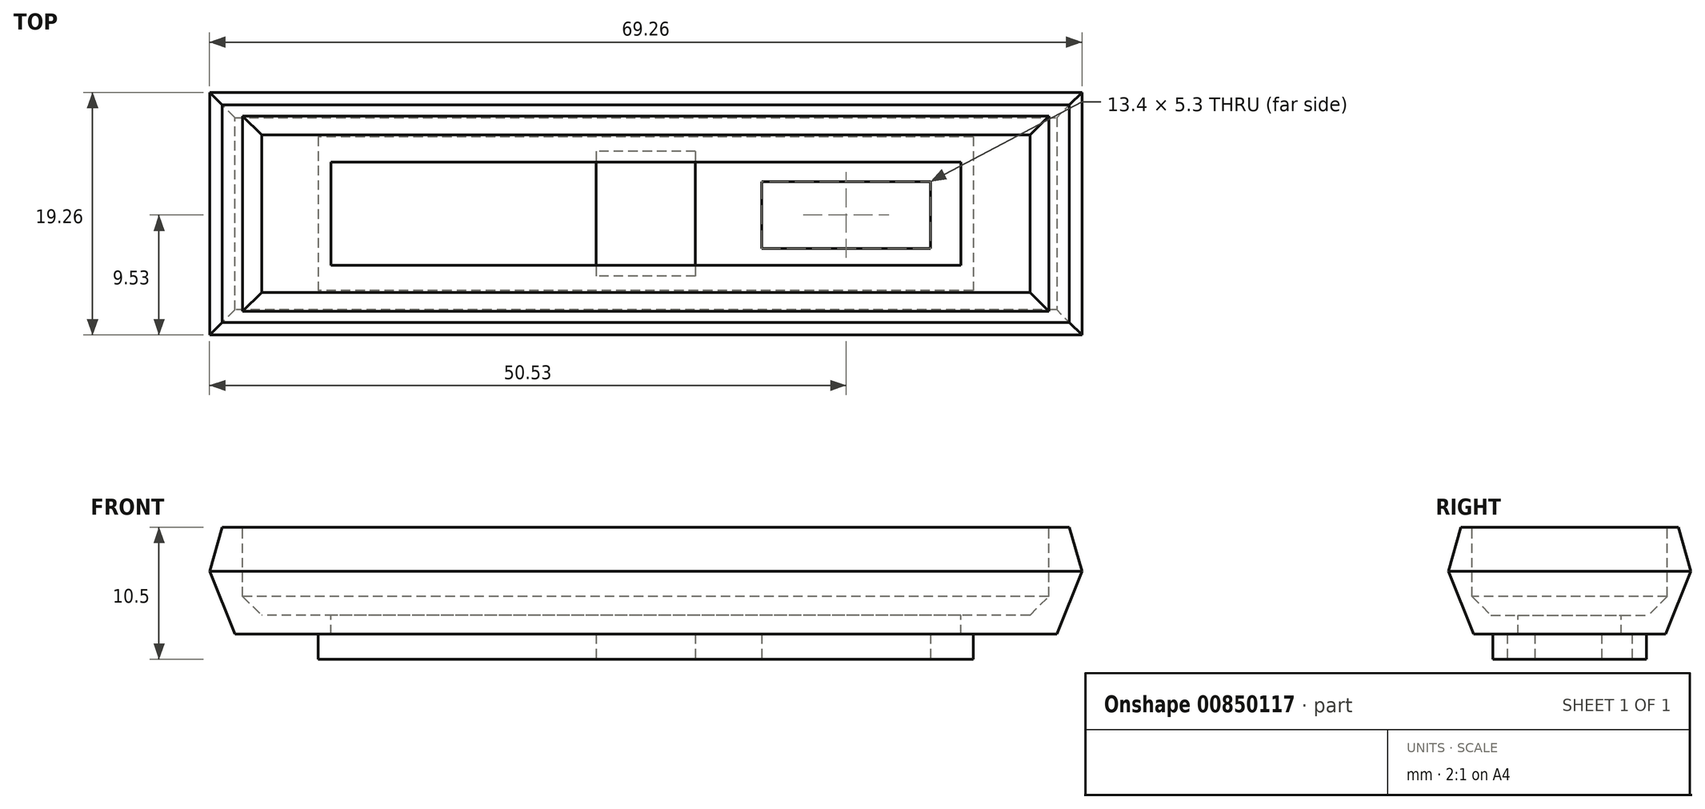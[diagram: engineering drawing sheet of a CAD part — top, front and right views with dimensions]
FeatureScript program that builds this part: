
annotation { "Feature Type Name" : "Feature", "Feature Type Description" : "" }
export const myFeature = defineFeature(function(context is Context, id is Id, definition is map)
    precondition{}
    {
        {
            var Q0;
            Q0=qCreatedBy(makeId("Top.planeOp"),FACE);
            var sketch = newSketch(context, id + "F0", { "sketchPlane" : qUnion([Q0])});
            skLineSegment(sketch, "E0.bottom", {"start": v(34.62, -9.62) * mm, "end": v(-34.62, -9.63) * mm});
            skLineSegment(sketch, "E0.top", {"start": v(34.62, 9.63) * mm, "end": v(-34.62, 9.62) * mm});
            skLineSegment(sketch, "E0.left", {"start": v(34.62, -9.62) * mm, "end": v(34.62, 9.63) * mm});
            skLineSegment(sketch, "E0.right", {"start": v(-34.62, -9.63) * mm, "end": v(-34.62, 9.62) * mm});
            skPoint(sketch, "E0.middle", {"position": v(0, 0) * mm});
            skSolve(sketch);
        }
        {
            var Q0;
            Q0=makeQuery(id+"F0.imprint","IMPRINT",FACE,{"disambiguationData":[TD([[makeQuery(id+"F0.imprint","IMPRINT",EDGE,{"derivedFrom":sQuery(id+"F0.wireOp",EDGE,"E0.bottom")}),-1.0]])]});
            extrude(context, id + "F1", {"entities" : qUnion([Q0]), "depth" : 8.5 * mm, "offsetDistance" : 25 * mm});
        }
        {
            var Q0;
            Q0=makeQuery(id+"F1.opExtrude","CAP_FACE",FACE,{"disambiguationData":[OSD([sQuery(id+"F0.wireOp",EDGE,"E0.bottom"),sQuery(id+"F0.wireOp",EDGE,"E0.top"),sQuery(id+"F0.wireOp",EDGE,"E0.left"),sQuery(id+"F0.wireOp",EDGE,"E0.right")])],"isStart":false});
            var sketch = newSketch(context, id + "F2", { "sketchPlane" : qUnion([Q0])});
            skLineSegment(sketch, "E1.bottom", {"start": v(32, -7.75) * mm, "end": v(-32, -7.75) * mm});
            skLineSegment(sketch, "E1.top", {"start": v(32, 7.75) * mm, "end": v(-32, 7.75) * mm});
            skLineSegment(sketch, "E1.left", {"start": v(32, -7.75) * mm, "end": v(32, 7.75) * mm});
            skLineSegment(sketch, "E1.right", {"start": v(-32, -7.75) * mm, "end": v(-32, 7.75) * mm});
            skPoint(sketch, "E1.middle", {"position": v(0, 0) * mm});
            skLineSegment(sketch, "E2.bottom", {"start": v(33, -8.75) * mm, "end": v(-33, -8.75) * mm});
            skLineSegment(sketch, "E2.top", {"start": v(33, 8.75) * mm, "end": v(-33, 8.75) * mm});
            skLineSegment(sketch, "E2.left", {"start": v(33, -8.75) * mm, "end": v(33, 8.75) * mm});
            skLineSegment(sketch, "E2.right", {"start": v(-33, -8.75) * mm, "end": v(-33, 8.75) * mm});
            skSolve(sketch);
        }
        {
            var Q0;
            Q0=makeQuery(id+"F1.opExtrude","CAP_EDGE",EDGE,{"disambiguationData":[OSD([sQuery(id+"F0.wireOp",EDGE,"E0.right")])],"isStart":false});
            var Q1;
            Q1=makeQuery(id+"F1.opExtrude","CAP_EDGE",EDGE,{"disambiguationData":[OSD([sQuery(id+"F0.wireOp",EDGE,"E0.bottom")])],"isStart":false});
            var Q2;
            Q2=makeQuery(id+"F1.opExtrude","CAP_EDGE",EDGE,{"disambiguationData":[OSD([sQuery(id+"F0.wireOp",EDGE,"E0.left")])],"isStart":false});
            var Q3;
            Q3=makeQuery(id+"F1.opExtrude","CAP_EDGE",EDGE,{"disambiguationData":[OSD([sQuery(id+"F0.wireOp",EDGE,"E0.top")])],"isStart":false});
            chamfer(context, id + "F3", {"entities" : qUnion([Q0, Q1, Q2, Q3]), "chamferType" : ChamferType.TWO_OFFSETS, "width1" : 3.5 * mm, "oppositeDirection" : false, "width2" : 1 * mm, "tangentPropagation" : true});
        }
        {
            var Q0;
            Q0=makeQuery(id+"F1.opExtrude","CAP_EDGE",EDGE,{"disambiguationData":[OSD([sQuery(id+"F0.wireOp",EDGE,"E0.right")])],"isStart":true});
            var Q1;
            Q1=makeQuery(id+"F1.opExtrude","CAP_EDGE",EDGE,{"disambiguationData":[OSD([sQuery(id+"F0.wireOp",EDGE,"E0.bottom")])],"isStart":true});
            var Q2;
            Q2=makeQuery(id+"F1.opExtrude","CAP_EDGE",EDGE,{"disambiguationData":[OSD([sQuery(id+"F0.wireOp",EDGE,"E0.top")])],"isStart":true});
            var Q3;
            Q3=makeQuery(id+"F1.opExtrude","CAP_EDGE",EDGE,{"disambiguationData":[OSD([sQuery(id+"F0.wireOp",EDGE,"E0.left")])],"isStart":true});
            chamfer(context, id + "F4", {"entities" : qUnion([Q0, Q1, Q2, Q3]), "chamferType" : ChamferType.TWO_OFFSETS, "width1" : 2 * mm, "oppositeDirection" : false, "width2" : 5 * mm, "tangentPropagation" : true});
        }
        {
            var Q0;
            Q0=makeQuery(id+"F2.imprint","IMPRINT",FACE,{"disambiguationData":[TD([[makeQuery(id+"F2.imprint","IMPRINT",EDGE,{"derivedFrom":sQuery(id+"F2.wireOp",EDGE,"E1.bottom")}),-1.0]])]});
            extrude(context, id + "F5", {"entities" : qUnion([Q0]), "operationType" : NewBodyOperationType.REMOVE, "oppositeDirection" : true, "depth" : 7 * mm, "offsetDistance" : 25 * mm});
        }
        {
            var Q0;
            Q0=makeQuery(id+"F1.opExtrude","CAP_FACE",FACE,{"disambiguationData":[OSD([sQuery(id+"F0.wireOp",EDGE,"E0.bottom"),sQuery(id+"F0.wireOp",EDGE,"E0.top"),sQuery(id+"F0.wireOp",EDGE,"E0.left"),sQuery(id+"F0.wireOp",EDGE,"E0.right")])],"isStart":true});
            var sketch = newSketch(context, id + "F6", { "sketchPlane" : qUnion([Q0])});
            skLineSegment(sketch, "E3.bottom", {"start": v(26, -6.1) * mm, "end": v(-26, -6.1) * mm});
            skLineSegment(sketch, "E3.top", {"start": v(26, 6.1) * mm, "end": v(-26, 6.1) * mm});
            skLineSegment(sketch, "E3.left", {"start": v(26, -6.1) * mm, "end": v(26, 6.1) * mm});
            skLineSegment(sketch, "E3.right", {"start": v(-26, -6.1) * mm, "end": v(-26, 6.1) * mm});
            skPoint(sketch, "E3.middle", {"position": v(0, 0) * mm});
            skSolve(sketch);
        }
        {
            var Q0;
            Q0=makeQuery(id+"F6.imprint","IMPRINT",FACE,{"disambiguationData":[TD([[makeQuery(id+"F6.imprint","IMPRINT",EDGE,{"derivedFrom":sQuery(id+"F6.wireOp",EDGE,"E3.bottom")}),-1.0]])]});
            extrude(context, id + "F7", {"entities" : qUnion([Q0]), "operationType" : NewBodyOperationType.ADD, "depth" : 2 * mm, "offsetDistance" : 25 * mm});
        }
        {
            var Q0;
            Q0=makeQuery(id+"F7.opExtrude","CAP_FACE",FACE,{"disambiguationData":[OSD([sQuery(id+"F6.wireOp",EDGE,"E3.bottom"),sQuery(id+"F6.wireOp",EDGE,"E3.top"),sQuery(id+"F6.wireOp",EDGE,"E3.left"),sQuery(id+"F6.wireOp",EDGE,"E3.right")])],"isStart":false});
            var sketch = newSketch(context, id + "F8", { "sketchPlane" : qUnion([Q0])});
            skLineSegment(sketch, "E4.bottom", {"start": v(3.95, -4.95) * mm, "end": v(-3.95, -4.95) * mm});
            skLineSegment(sketch, "E4.top", {"start": v(3.95, 4.95) * mm, "end": v(-3.95, 4.95) * mm});
            skLineSegment(sketch, "E4.left", {"start": v(3.95, -4.95) * mm, "end": v(3.95, 4.95) * mm});
            skLineSegment(sketch, "E4.right", {"start": v(-3.95, -4.95) * mm, "end": v(-3.95, 4.95) * mm});
            skPoint(sketch, "E4.middle", {"position": v(0, 0) * mm});
            skLineSegment(sketch, "E5.bottom", {"start": v(-26, 6.1) * mm, "end": v(-22.6, 6.1) * mm});
            skLineSegment(sketch, "E5.top", {"start": v(-26, -6.1) * mm, "end": v(-22.6, -6.1) * mm});
            skLineSegment(sketch, "E5.left", {"start": v(-26, 6.1) * mm, "end": v(-26, -6.1) * mm});
            skLineSegment(sketch, "E5.right", {"start": v(-22.6, 6.1) * mm, "end": v(-22.6, -6.1) * mm});
            skLineSegment(sketch, "E6.bottom", {"start": v(-22.6, 6.1) * mm, "end": v(15.72, 6.1) * mm});
            skLineSegment(sketch, "E6.top", {"start": v(-22.6, 2.75) * mm, "end": v(15.72, 2.75) * mm});
            skLineSegment(sketch, "E6.left", {"start": v(-22.6, 6.1) * mm, "end": v(-22.6, 2.75) * mm});
            skLineSegment(sketch, "E6.right", {"start": v(15.72, 6.1) * mm, "end": v(15.72, 2.75) * mm});
            skLineSegment(sketch, "E7.bottom", {"start": v(26, 6.1) * mm, "end": v(22.6, 6.1) * mm});
            skLineSegment(sketch, "E7.top", {"start": v(26, -6.1) * mm, "end": v(22.6, -6.1) * mm});
            skLineSegment(sketch, "E7.left", {"start": v(26, 6.1) * mm, "end": v(26, -6.1) * mm});
            skLineSegment(sketch, "E7.right", {"start": v(22.6, 6.1) * mm, "end": v(22.6, -6.1) * mm});
            skLineSegment(sketch, "E8.bottom", {"start": v(15.72, 2.75) * mm, "end": v(22.6, 2.75) * mm});
            skLineSegment(sketch, "E8.top", {"start": v(15.72, 6.1) * mm, "end": v(22.6, 6.1) * mm});
            skLineSegment(sketch, "E8.left", {"start": v(15.72, 2.75) * mm, "end": v(15.72, 6.1) * mm});
            skLineSegment(sketch, "E8.right", {"start": v(22.6, 2.75) * mm, "end": v(22.6, 6.1) * mm});
            skLineSegment(sketch, "E9.bottom", {"start": v(22.6, 2.75) * mm, "end": v(9.2, 2.75) * mm});
            skLineSegment(sketch, "E9.top", {"start": v(22.6, -2.55) * mm, "end": v(9.2, -2.55) * mm});
            skLineSegment(sketch, "E9.left", {"start": v(22.6, 2.75) * mm, "end": v(22.6, -2.55) * mm});
            skLineSegment(sketch, "E9.right", {"start": v(9.2, 2.75) * mm, "end": v(9.2, -2.55) * mm});
            skLineSegment(sketch, "E10.bottom", {"start": v(-22.6, 2.75) * mm, "end": v(-9.2, 2.75) * mm});
            skLineSegment(sketch, "E10.top", {"start": v(-22.6, -2.65) * mm, "end": v(-9.2, -2.65) * mm});
            skLineSegment(sketch, "E10.left", {"start": v(-22.6, 2.75) * mm, "end": v(-22.6, -2.65) * mm});
            skLineSegment(sketch, "E10.right", {"start": v(-9.2, 2.75) * mm, "end": v(-9.2, -2.65) * mm});
            skSolve(sketch);
        }
        {
            var Q0;
            Q0=makeQuery(id+"F8.imprint","IMPRINT",FACE,{"disambiguationData":[TD([[makeQuery(id+"F8.imprint","IMPRINT",EDGE,{"derivedFrom":sQuery(id+"F8.wireOp",EDGE,"E4.bottom")}),-1.0]])]});
            var Q1;
            {var subQ0=sQuery(id+"F8.wireOp",EDGE,"E4.top");Q1=makeQuery(id+"F8.imprint","IMPRINT",FACE,{"disambiguationData":[TD([[makeQuery(id+"F8.imprint","IMPRINT",EDGE,{"derivedFrom":subQ0}),1.0]])]});}
            extrude(context, id + "F9", {"entities" : qUnion([Q0, Q1]), "operationType" : NewBodyOperationType.REMOVE, "oppositeDirection" : true, "depth" : 2 * mm, "offsetDistance" : 25 * mm});
        }
        {
            var Q0;
            Q0=makeQuery(id+"F8.imprint","IMPRINT",FACE,{"disambiguationData":[TD([[makeQuery(id+"F8.imprint","IMPRINT",EDGE,{"derivedFrom":sQuery(id+"F8.wireOp",EDGE,"E10.bottom")}),-1.0]])]});
            var Q1;
            Q1=makeQuery(id+"F8.imprint","IMPRINT",FACE,{"disambiguationData":[TD([[makeQuery(id+"F8.imprint","IMPRINT",EDGE,{"derivedFrom":sQuery(id+"F8.wireOp",EDGE,"E9.top")}),-1.0]])]});
            extrude(context, id + "F10", {"entities" : qUnion([Q0, Q1]), "operationType" : NewBodyOperationType.REMOVE, "oppositeDirection" : true, "depth" : 25 * mm, "offsetDistance" : 25 * mm});
        }
        {
            var Q0;
            Q0=makeQuery(id+"F5.boolean.opBoolean","COPY",FACE,{"derivedFrom":makeQuery(id+"F5.opExtrude","CAP_FACE",FACE,{"disambiguationData":[OSD([sQuery(id+"F2.wireOp",EDGE,"E1.bottom"),sQuery(id+"F2.wireOp",EDGE,"E1.top"),sQuery(id+"F2.wireOp",EDGE,"E1.left"),sQuery(id+"F2.wireOp",EDGE,"E1.right")])],"isStart":false})});
            var sketch = newSketch(context, id + "F11", { "sketchPlane" : qUnion([Q0])});
            skLineSegment(sketch, "E11.bottom", {"start": v(25, -4.1) * mm, "end": v(-25, -4.1) * mm});
            skLineSegment(sketch, "E11.top", {"start": v(25, 4.1) * mm, "end": v(-25, 4.1) * mm});
            skLineSegment(sketch, "E11.left", {"start": v(25, -4.1) * mm, "end": v(25, 4.1) * mm});
            skLineSegment(sketch, "E11.right", {"start": v(-25, -4.1) * mm, "end": v(-25, 4.1) * mm});
            skPoint(sketch, "E11.middle", {"position": v(0, 0) * mm});
            skSolve(sketch);
        }
        {
            var Q0;
            Q0=makeQuery(id+"F11.imprint","IMPRINT",FACE,{"disambiguationData":[TD([[makeQuery(id+"F11.imprint","IMPRINT",EDGE,{"derivedFrom":sQuery(id+"F11.wireOp",EDGE,"E11.bottom")}),-1.0]])]});
            extrude(context, id + "F12", {"entities" : qUnion([Q0]), "operationType" : NewBodyOperationType.REMOVE, "oppositeDirection" : true, "depth" : 1.5 * mm, "offsetDistance" : 25 * mm});
        }
        {
            var Q0;
            Q0=makeQuery(id+"F5.boolean.opBoolean","COPY",EDGE,{"derivedFrom":makeQuery(id+"F5.opExtrude","CAP_EDGE",EDGE,{"disambiguationData":[OSD([sQuery(id+"F2.wireOp",EDGE,"E1.right")])],"isStart":false})});
            var Q1;
            Q1=makeQuery(id+"F5.boolean.opBoolean","COPY",EDGE,{"derivedFrom":makeQuery(id+"F5.opExtrude","CAP_EDGE",EDGE,{"disambiguationData":[OSD([sQuery(id+"F2.wireOp",EDGE,"E1.top")])],"isStart":false})});
            var Q2;
            Q2=makeQuery(id+"F5.boolean.opBoolean","COPY",EDGE,{"derivedFrom":makeQuery(id+"F5.opExtrude","CAP_EDGE",EDGE,{"disambiguationData":[OSD([sQuery(id+"F2.wireOp",EDGE,"E1.left")])],"isStart":false})});
            var Q3;
            Q3=makeQuery(id+"F5.boolean.opBoolean","COPY",EDGE,{"derivedFrom":makeQuery(id+"F5.opExtrude","CAP_EDGE",EDGE,{"disambiguationData":[OSD([sQuery(id+"F2.wireOp",EDGE,"E1.bottom")])],"isStart":false})});
            chamfer(context, id + "F13", {"entities" : qUnion([Q0, Q1, Q2, Q3]), "width" : 1.5 * mm, "tangentPropagation" : true});
        }
    });
